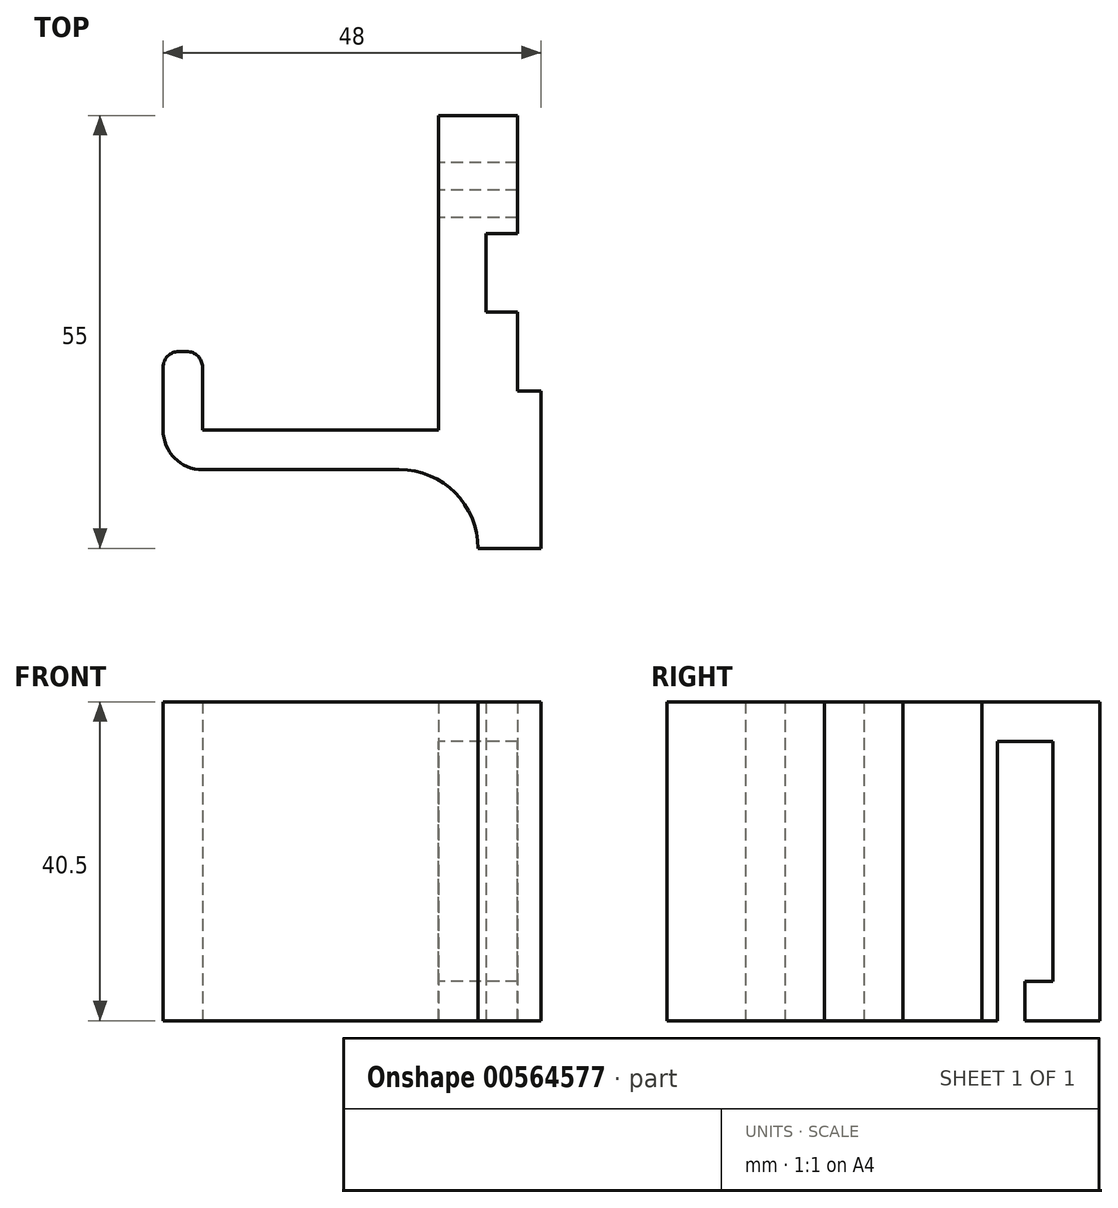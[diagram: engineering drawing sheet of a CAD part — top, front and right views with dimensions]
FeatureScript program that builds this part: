
annotation { "Feature Type Name" : "Feature", "Feature Type Description" : "" }
export const myFeature = defineFeature(function(context is Context, id is Id, definition is map)
    precondition{}
    {
        {
            var Q0;
            Q0=qCreatedBy(makeId("Top.planeOp"),FACE);
            var sketch = newSketch(context, id + "F0", { "sketchPlane" : qUnion([Q0])});
            skLineSegment(sketch, "E0.bottom", {"start": v(-18.78, 29.12) * mm, "end": v(-8.78, 29.12) * mm});
            skLineSegment(sketch, "E0.left", {"start": v(-18.78, 29.12) * mm, "end": v(-18.78, -10.88) * mm});
            skLineSegment(sketch, "E1.top", {"start": v(-48.78, -10.88) * mm, "end": v(-18.78, -10.88) * mm});
            skLineSegment(sketch, "E2", {"start": v(-48.78, -10.88) * mm, "end": v(-48.78, -2.88) * mm});
            skLineSegment(sketch, "E3", {"start": v(-50.78, -0.88) * mm, "end": v(-51.78, -0.88) * mm});
            skLineSegment(sketch, "E4", {"start": v(-53.78, -2.88) * mm, "end": v(-53.78, -10.88) * mm});
            skLineSegment(sketch, "E5", {"start": v(-8.78, 16.12) * mm, "end": v(-8.78, 14.12) * mm});
            skLineSegment(sketch, "E6", {"start": v(-8.78, 16.12) * mm, "end": v(-8.78, 29.12) * mm});
            skLineSegment(sketch, "E7", {"start": v(-8.78, 14.12) * mm, "end": v(-12.78, 14.12) * mm});
            skLineSegment(sketch, "E8", {"start": v(-12.78, 4.12) * mm, "end": v(-12.78, 14.12) * mm});
            skLineSegment(sketch, "E9", {"start": v(-8.78, 4.12) * mm, "end": v(-12.78, 4.12) * mm});
            skLineSegment(sketch, "E10", {"start": v(-8.78, 4.12) * mm, "end": v(-8.78, -5.88) * mm});
            skLineSegment(sketch, "E11", {"start": v(-8.78, -5.88) * mm, "end": v(-5.78, -5.88) * mm});
            skLineSegment(sketch, "E12", {"start": v(-5.78, -5.88) * mm, "end": v(-5.78, -25.88) * mm});
            skLineSegment(sketch, "E13", {"start": v(-13.78, -25.88) * mm, "end": v(-5.78, -25.88) * mm});
            skArc(sketch, "E14.filletArc", {"start": v(-53.78, -10.88) * mm, "mid": v(-52.31, -14.41) * mm, "end": v(-48.78, -15.88) * mm});
            skPoint(sketch, "E15.visualSharp", {"position": v(-53.78, -0.88) * mm});
            skArc(sketch, "E15.filletArc", {"start": v(-51.78, -0.88) * mm, "mid": v(-53.2, -1.46) * mm, "end": v(-53.78, -2.88) * mm});
            skPoint(sketch, "E16.visualSharp", {"position": v(-48.78, -0.88) * mm});
            skArc(sketch, "E16.filletArc", {"start": v(-48.78, -2.88) * mm, "mid": v(-49.36, -1.46) * mm, "end": v(-50.78, -0.88) * mm});
            skLineSegment(sketch, "E17", {"start": v(-48.78, -15.88) * mm, "end": v(-23.78, -15.88) * mm});
            skLineSegment(sketch, "E18", {"start": v(-13.78, -25.88) * mm, "end": v(-13.78, -25.88) * mm});
            skPoint(sketch, "E19.visualSharp", {"position": v(-13.78, -15.88) * mm});
            skArc(sketch, "E19.filletArc", {"start": v(-13.78, -25.88) * mm, "mid": v(-16.7, -18.8) * mm, "end": v(-23.78, -15.88) * mm});
            skSolve(sketch);
        }
        {
            var Q0;
            Q0 = qSketchRegion(id + "F0", true);
            var Q1;
            Q1=makeQuery(id+"F0.imprint","IMPRINT",FACE,{"disambiguationData":[TD([[makeQuery(id+"F0.imprint","IMPRINT",EDGE,{"derivedFrom":sQuery(id+"F0.wireOp",EDGE,"E0.bottom")}),-1.0]])]});
            extrude(context, id + "F1", {"entities" : qUnion([Q0, Q1]), "flatOperationType" : FlatOperationType.REMOVE, "depth" : 40.5 * mm, "offsetDistance" : 25 * mm, "domain" : OperationDomain.MODEL});
        }
        {
            var Q0;
            Q0=makeQuery(id+"F1.opExtrude","SWEPT_FACE",FACE,{"disambiguationData":[OSD([sQuery(id+"F0.wireOp",EDGE,"E0.left")])]});
            var sketch = newSketch(context, id + "F2", { "sketchPlane" : qUnion([Q0])});
            skLineSegment(sketch, "E20.top", {"start": v(-29.12, 0) * mm, "end": v(-19.62, 0) * mm});
            skLineSegment(sketch, "E20.left", {"start": v(-29.12, 40.5) * mm, "end": v(-29.12, 0) * mm});
            skLineSegment(sketch, "E21", {"start": v(-19.62, 0) * mm, "end": v(-19.62, 5) * mm});
            skLineSegment(sketch, "E22", {"start": v(-19.62, 5) * mm, "end": v(-23.12, 5) * mm});
            skLineSegment(sketch, "E23", {"start": v(-23.12, 5) * mm, "end": v(-23.12, 35.5) * mm});
            skLineSegment(sketch, "E24.trimOffspring", {"start": v(-19.62, 5) * mm, "end": v(-19.62, 0) * mm});
            skLineSegment(sketch, "E25", {"start": v(-16.12, 0) * mm, "end": v(-16.12, 35.5) * mm});
            skLineSegment(sketch, "E26", {"start": v(-23.12, 35.5) * mm, "end": v(-16.12, 35.5) * mm});
            skSolve(sketch);
        }
        {
            var Q0;
            Q0 = qSketchRegion(id + "F2", true);
            var Q1;
            Q1=makeQuery(id+"F2.imprint","IMPRINT",FACE,{"disambiguationData":[TD([[makeQuery(id+"F2.imprint","IMPRINT",EDGE,{"derivedFrom":sQuery(id+"F2.wireOp",EDGE,"E22")}),-1.0]])]});
            extrude(context, id + "F3", {"entities" : qUnion([Q0, Q1]), "operationType" : NewBodyOperationType.REMOVE, "flatOperationType" : FlatOperationType.REMOVE, "oppositeDirection" : true, "depth" : 10 * mm, "offsetDistance" : 25 * mm, "domain" : OperationDomain.MODEL});
        }
    });
